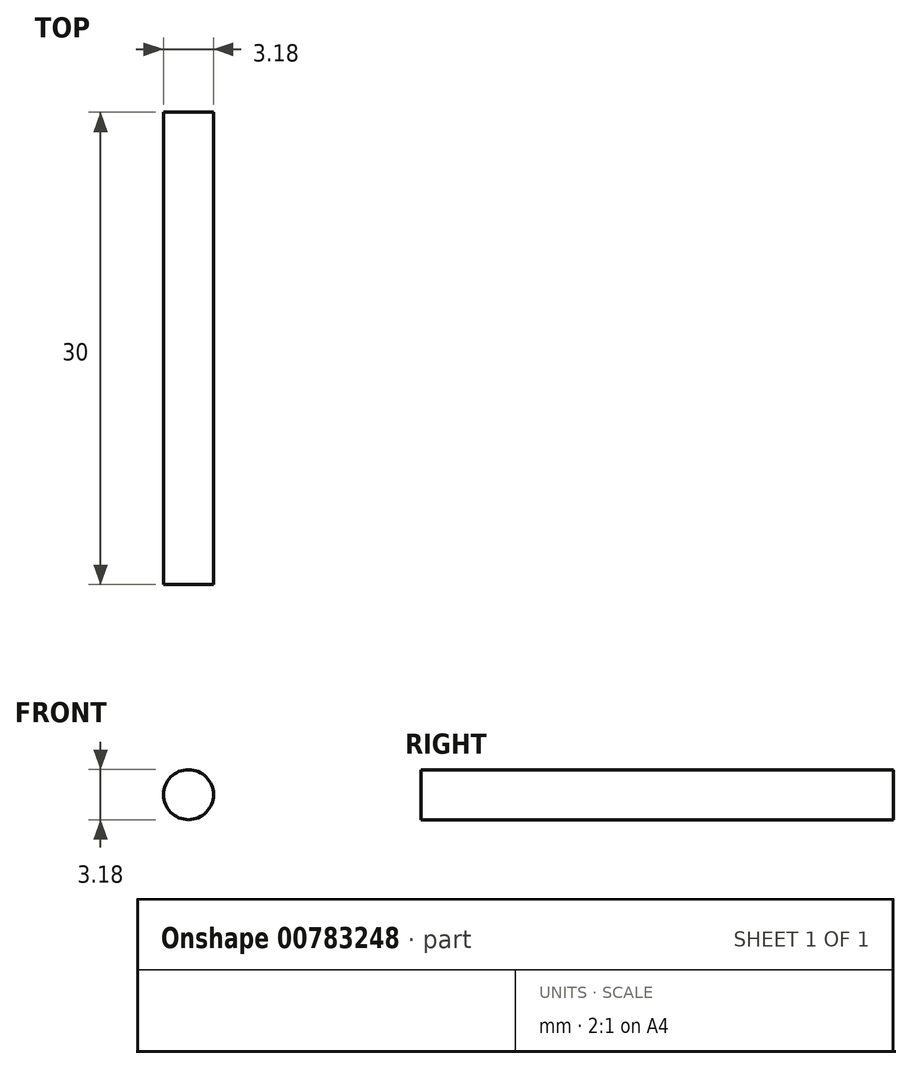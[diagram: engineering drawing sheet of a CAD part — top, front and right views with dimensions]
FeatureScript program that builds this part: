
annotation { "Feature Type Name" : "Feature", "Feature Type Description" : "" }
export const myFeature = defineFeature(function(context is Context, id is Id, definition is map)
    precondition{}
    {
        {
            var Q0;
            Q0=qCreatedBy(makeId("Front.planeOp"),FACE);
            var sketch = newSketch(context, id + "F0", { "sketchPlane" : qUnion([Q0])});
            skCircle(sketch, "E0", {"center": v(-31.35, 23.54) * mm, "radius": 1.59 * mm});
            skSolve(sketch);
        }
        {
            var Q0;
            Q0=makeQuery(id+"F0.imprint","IMPRINT",FACE,{"disambiguationData":[TD([[makeQuery(id+"F0.imprint","IMPRINT",EDGE,{"derivedFrom":sQuery(id+"F0.wireOp",EDGE,"E0")}),1.0]])]});
            extrude(context, id + "F1", {"entities" : qUnion([Q0]), "depth" : 30 * mm, "offsetDistance" : 25.4 * mm});
        }
    });
